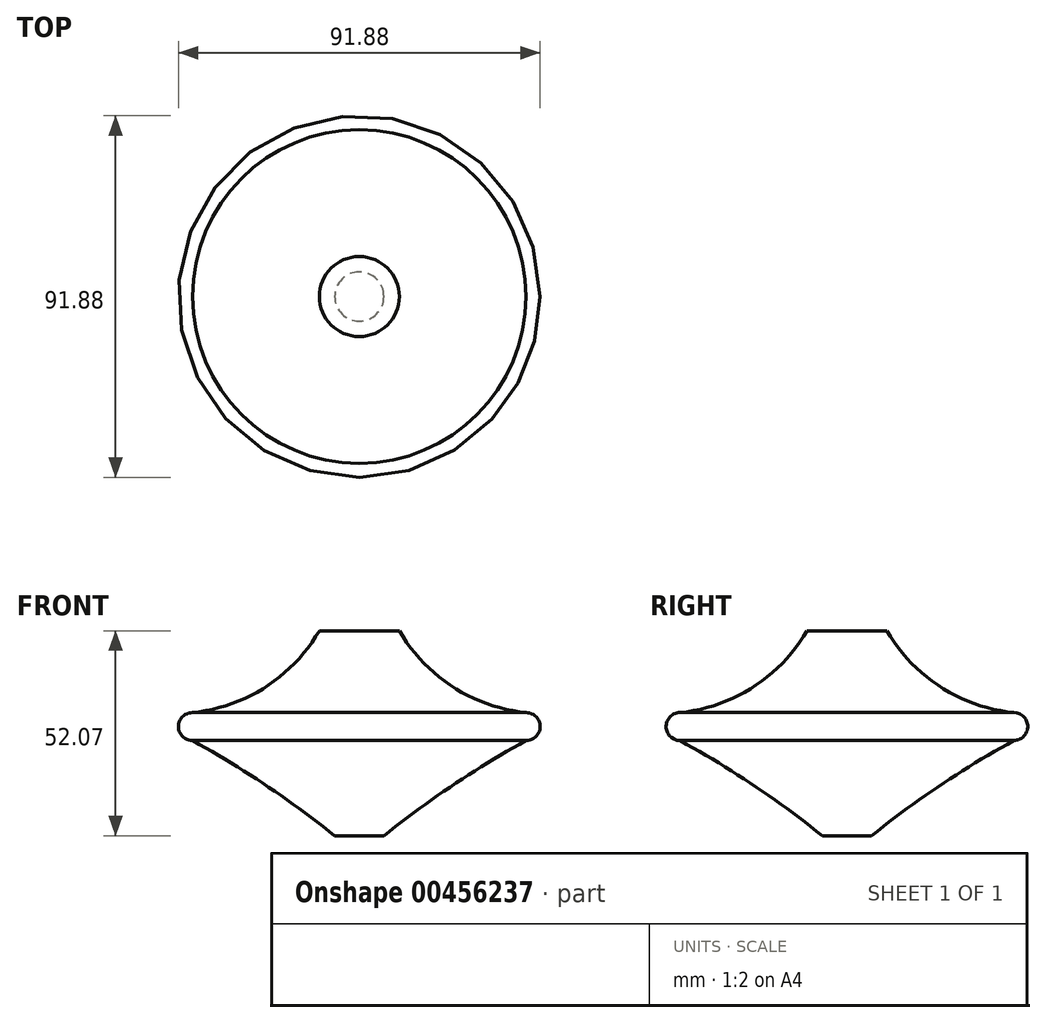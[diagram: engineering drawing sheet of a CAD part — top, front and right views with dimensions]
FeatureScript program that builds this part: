
annotation { "Feature Type Name" : "Feature", "Feature Type Description" : "" }
export const myFeature = defineFeature(function(context is Context, id is Id, definition is map)
    precondition{}
    {
        {
            var Q0;
            Q0=qCreatedBy(makeId("Front.planeOp"),FACE);
            var sketch = newSketch(context, id + "F0", { "sketchPlane" : qUnion([Q0])});
            skLineSegment(sketch, "E0", {"start": v(0, 0) * mm, "end": v(6.25, 0) * mm});
            skLineSegment(sketch, "E1", {"start": v(10.16, 52.07) * mm, "end": v(0, 52.07) * mm});
            skLineSegment(sketch, "E2", {"start": v(0, 52.07) * mm, "end": v(0, 0) * mm});
            skArc(sketch, "E3", {"start": v(10.16, 52.07) * mm, "mid": v(23.78, 37.82) * mm, "end": v(42.38, 31.31) * mm});
            skArc(sketch, "E4", {"start": v(42.38, 24.2) * mm, "mid": v(45.94, 27.76) * mm, "end": v(42.38, 31.31) * mm});
            skArc(sketch, "E5", {"start": v(42.38, 24.2) * mm, "mid": v(23.8, 12.87) * mm, "end": v(6.25, 0) * mm});
            skSolve(sketch);
        }
        {
            var Q0;
            Q0=makeQuery(id+"F0.imprint","IMPRINT",FACE,{"disambiguationData":[TD([[makeQuery(id+"F0.imprint","IMPRINT",EDGE,{"derivedFrom":sQuery(id+"F0.wireOp",EDGE,"E0")}),1.0]])]});
            var Q1;
            Q1=sQuery(id+"F0.wireOp",EDGE,"E2");
            revolve(context, id + "F1", {"entities" : qUnion([Q0]), "axis" : qUnion([Q1]), "revolveType" : RevolveType.FULL});
        }
    });
